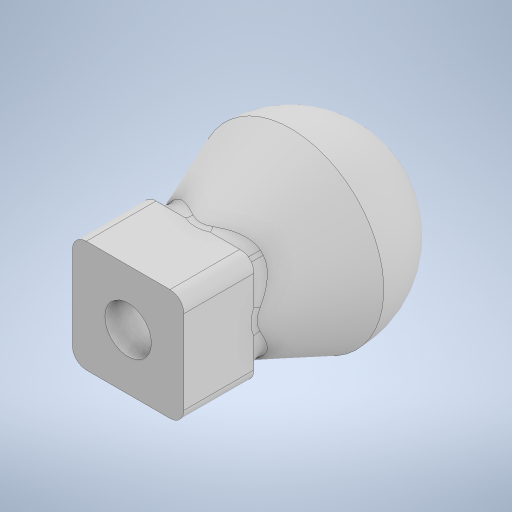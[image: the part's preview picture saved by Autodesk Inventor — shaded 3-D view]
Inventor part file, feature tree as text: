
AUTODESK INVENTOR PART (.ipt)
format: ipt  version: 2024.3 (Build 283343000, 343)  size: 377,856 bytes
history: native  units: mm
features: sketch x2, other x1, revolve x1, extrude x1, fillet x1
ambient origin geometry x8: Origin, YZ Plane, XZ Plane, XY Plane, X Axis, Y Axis, Z Axis, Center Point
bodies: Body1 (feature_tree)
feature tree (6):
  other  "ソリッド1"
  revolve  "回転1"
  extrude  "押し出し2"  Depth=20.0mm
  fillet  "フィレット1"  [1 undecoded]
  sketch  "スケッチ4"
  sketch  "スケッチ5"
note: 1 required parameter value undecoded (feature->parameter linkage not recoverable at this tier; creation-order binding heuristic only, values carry confidence <= 0.55)
